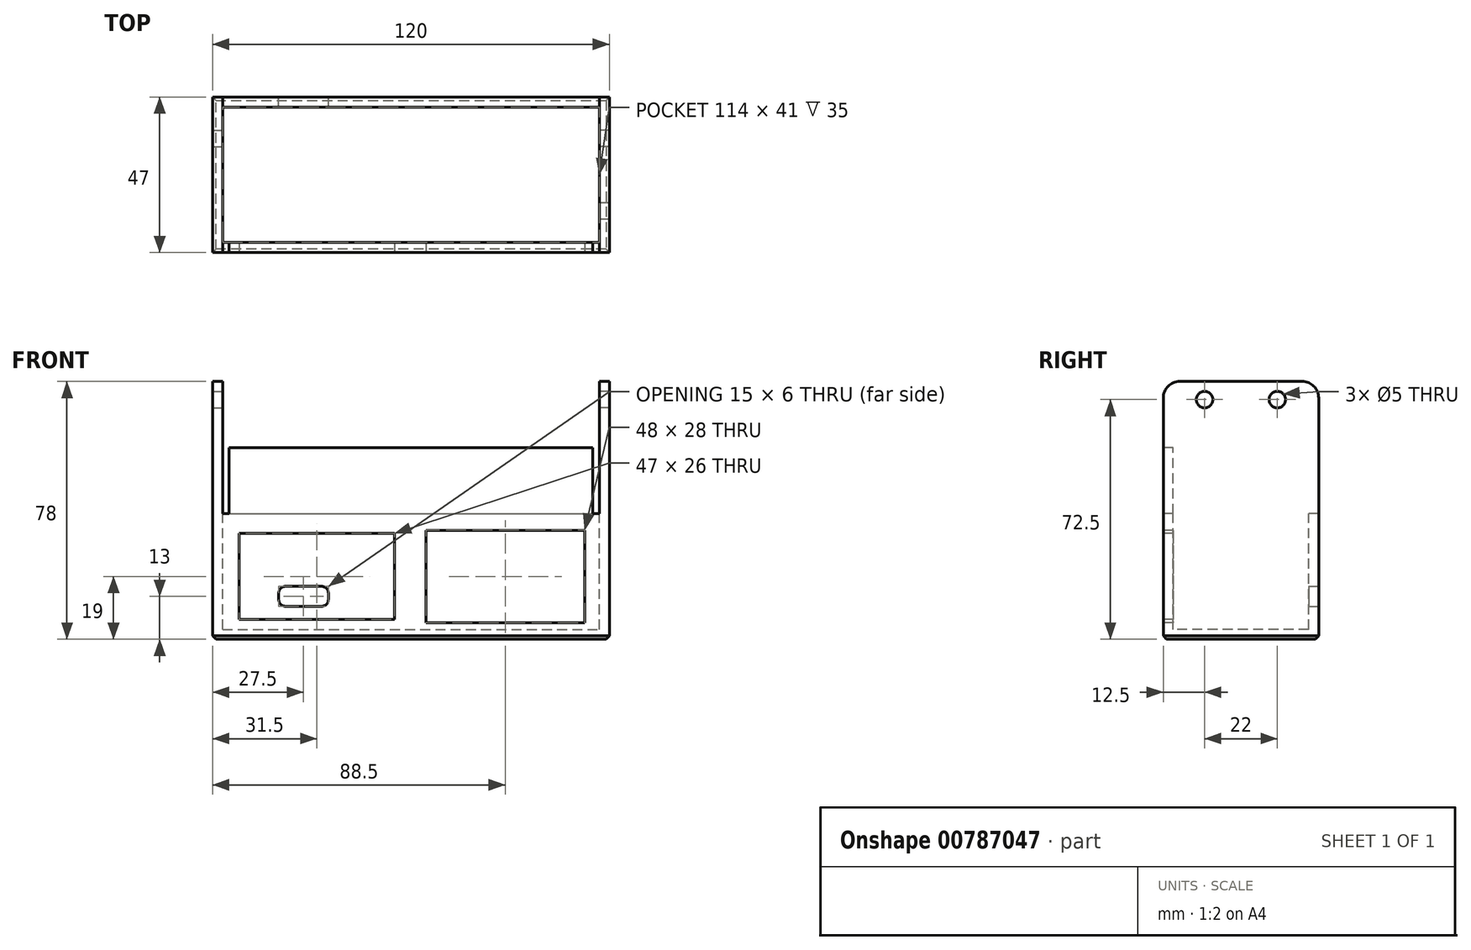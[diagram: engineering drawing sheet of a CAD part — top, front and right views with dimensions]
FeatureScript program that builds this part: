
annotation { "Feature Type Name" : "Feature", "Feature Type Description" : "" }
export const myFeature = defineFeature(function(context is Context, id is Id, definition is map)
    precondition{}
    {
        {
            assignVariable(context, id + "F0", {"name" : "wall", "anyValue" : 3});
        }
        {
            assignVariable(context, id + "F1", {"name" : "width", "anyValue" : 114});
        }
        {
            var Q0;
            Q0=qCreatedBy(makeId("Right.planeOp"),FACE);
            var sketch = newSketch(context, id + "F2", { "sketchPlane" : qUnion([Q0])});
            skLineSegment(sketch, "E0.bottom", {"start": v(17.5, 40) * mm, "end": v(-19.5, 40) * mm});
            skLineSegment(sketch, "E0.top", {"start": v(22.5, -38) * mm, "end": v(-24.5, -38) * mm});
            skLineSegment(sketch, "E0.left", {"start": v(22.5, 35) * mm, "end": v(22.5, -38) * mm});
            skLineSegment(sketch, "E0.right", {"start": v(-24.5, 35) * mm, "end": v(-24.5, -38) * mm});
            skCircle(sketch, "E1", {"center": v(10, 34.5) * mm, "radius": 2.5 * mm});
            skCircle(sketch, "E2", {"center": v(-12, 34.5) * mm, "radius": 2.5 * mm});
            skPoint(sketch, "E3.visualSharp", {"position": v(-24.5, 40) * mm});
            skArc(sketch, "E3.filletArc", {"start": v(-19.5, 40) * mm, "mid": v(-23.04, 38.54) * mm, "end": v(-24.5, 35) * mm});
            skPoint(sketch, "E4.visualSharp", {"position": v(22.5, 40) * mm});
            skArc(sketch, "E4.filletArc", {"start": v(22.5, 35) * mm, "mid": v(21.04, 38.54) * mm, "end": v(17.5, 40) * mm});
            skSolve(sketch);
        }
        {
            var Q0;
            Q0=qSketchRegion(id+"F2",true);
            extrude(context, id + "F3", {"entities" : qUnion([Q0]), "depth" : (getVariable(context, 'wall')) * mm, "offsetDistance" : 25 * mm});
        }
        {
            var Q0;
            Q0=qCreatedBy(makeId("Right.planeOp"),FACE);
            var sketch = newSketch(context, id + "F4", { "sketchPlane" : qUnion([Q0])});
            skLineSegment(sketch, "E5.bottom", {"start": v(22.5, -38) * mm, "end": v(-24.5, -38) * mm});
            skLineSegment(sketch, "E5.top", {"start": v(22.5, -35) * mm, "end": v(-24.5, -35) * mm});
            skLineSegment(sketch, "E5.left", {"start": v(22.5, -38) * mm, "end": v(22.5, -35) * mm});
            skLineSegment(sketch, "E5.right", {"start": v(-24.5, -38) * mm, "end": v(-24.5, -35) * mm});
            skLineSegment(sketch, "E6.bottom", {"start": v(-24.5, -38) * mm, "end": v(-21.5, -38) * mm});
            skLineSegment(sketch, "E6.top", {"start": v(-24.5, 0) * mm, "end": v(-21.5, 0) * mm});
            skLineSegment(sketch, "E6.left", {"start": v(-24.5, -38) * mm, "end": v(-24.5, 0) * mm});
            skLineSegment(sketch, "E6.right", {"start": v(-21.5, -38) * mm, "end": v(-21.5, 0) * mm});
            skLineSegment(sketch, "E7.bottom", {"start": v(22.5, -38) * mm, "end": v(19.5, -38) * mm});
            skLineSegment(sketch, "E7.top", {"start": v(22.5, 0) * mm, "end": v(19.5, 0) * mm});
            skLineSegment(sketch, "E7.left", {"start": v(22.5, -38) * mm, "end": v(22.5, 0) * mm});
            skLineSegment(sketch, "E7.right", {"start": v(19.5, -38) * mm, "end": v(19.5, 0) * mm});
            skSolve(sketch);
        }
        {
            var Q0;
            {var subQ0=sQuery(id+"F4.wireOp",EDGE,"E5.right");var subQ1=sQuery(id+"F4.wireOp",EDGE,"E5.bottom");var subQ9=sQuery(id+"F4.wireOp",EDGE,"E7.right");var subQ10=makeQuery(id+"F4.imprint","INTERSECT",VERTEX,{"derivedFrom":[subQ1,subQ9]});var subQ14=sQuery(id+"F4.wireOp",EDGE,"E5.left");var subQ16=sQuery(id+"F4.wireOp",EDGE,"E7.top");var subQ17=sQuery(id+"F4.wireOp",EDGE,"E6.top");Q0=qUnion([makeQuery(id+"F4.imprint","IMPRINT",FACE,{"disambiguationData":[TD([[makeQuery(id+"F4.imprint","IMPRINT",EDGE,{"derivedFrom":subQ17}),-1.0]])]}),makeQuery(id+"F4.imprint","IMPRINT",FACE,{"disambiguationData":[TD([[makeQuery(id+"F4.imprint","IMPRINT",EDGE,{"derivedFrom":subQ14}),1.0]])]}),makeQuery(id+"F4.imprint","IMPRINT",FACE,{"disambiguationData":[TD([[makeQuery(id+"F4.imprint","IMPRINT",EDGE,{"derivedFrom":subQ16}),1.0]])]}),makeQuery(id+"F4.imprint","IMPRINT",FACE,{"disambiguationData":[TD([[makeQuery(id+"F4.imprint","IMPRINT",EDGE,{"disambiguationData":[TD([[subQ10,-1.0]])],"derivedFrom":subQ1}),-1.0]])]}),makeQuery(id+"F4.imprint","IMPRINT",FACE,{"disambiguationData":[TD([[makeQuery(id+"F4.imprint","IMPRINT",EDGE,{"derivedFrom":subQ0}),-1.0]])]})]);}
            extrude(context, id + "F5", {"entities" : qUnion([Q0]), "operationType" : NewBodyOperationType.ADD, "oppositeDirection" : true, "depth" : (getVariable(context, 'width')) * mm, "offsetDistance" : 25 * mm});
        }
        {
            var Q0;
            Q0=makeQuery(id+"F5.opExtrude","CAP_FACE",FACE,{"disambiguationData":[OSD([sQuery(id+"F4.wireOp",EDGE,"E5.bottom"),sQuery(id+"F4.wireOp",EDGE,"E5.top"),sQuery(id+"F4.wireOp",EDGE,"E5.left"),sQuery(id+"F4.wireOp",EDGE,"E5.right"),sQuery(id+"F4.wireOp",EDGE,"E6.top"),sQuery(id+"F4.wireOp",EDGE,"E6.left"),sQuery(id+"F4.wireOp",EDGE,"E6.right"),sQuery(id+"F4.wireOp",EDGE,"E7.top"),sQuery(id+"F4.wireOp",EDGE,"E7.left"),sQuery(id+"F4.wireOp",EDGE,"E7.right")])],"isStart":false});
            var sketch = newSketch(context, id + "F6", { "sketchPlane" : qUnion([Q0])});
            skLineSegment(sketch, "E8.bottom", {"start": v(19.5, 40) * mm, "end": v(-17.5, 40) * mm});
            skLineSegment(sketch, "E8.top", {"start": v(24.5, -38) * mm, "end": v(-22.5, -38) * mm});
            skLineSegment(sketch, "E8.left", {"start": v(24.5, 35) * mm, "end": v(24.5, -38) * mm});
            skLineSegment(sketch, "E8.right", {"start": v(-22.5, 35) * mm, "end": v(-22.5, -38) * mm});
            skCircle(sketch, "E9", {"center": v(-10, 34.5) * mm, "radius": 2.5 * mm});
            skPoint(sketch, "E10.visualSharp", {"position": v(-22.5, 40) * mm});
            skArc(sketch, "E10.filletArc", {"start": v(-17.5, 40) * mm, "mid": v(-21.04, 38.54) * mm, "end": v(-22.5, 35) * mm});
            skPoint(sketch, "E11.visualSharp", {"position": v(24.5, 40) * mm});
            skArc(sketch, "E11.filletArc", {"start": v(24.5, 35) * mm, "mid": v(23.04, 38.54) * mm, "end": v(19.5, 40) * mm});
            skSolve(sketch);
        }
        {
            var Q0;
            Q0=qSketchRegion(id+"F6",true);
            extrude(context, id + "F7", {"entities" : qUnion([Q0]), "operationType" : NewBodyOperationType.ADD, "depth" : (getVariable(context, 'wall')) * mm, "offsetDistance" : 25 * mm});
        }
        {
            var Q0;
            Q0=makeQuery(id+"F7.boolean.opBoolean","MERGE",FACE,{"derivedFrom":[makeQuery(id+"F5.boolean.opBoolean","MERGE",FACE,{"derivedFrom":[makeQuery(id+"F3.opExtrude","SWEPT_FACE",FACE,{"disambiguationData":[OSD([sQuery(id+"F2.wireOp",EDGE,"E0.right")])]}),makeQuery(id+"F5.opExtrude","SWEPT_FACE",FACE,{"disambiguationData":[OSD([sQuery(id+"F4.wireOp",EDGE,"E5.right"),sQuery(id+"F4.wireOp",EDGE,"E6.left")])]})]}),makeQuery(id+"F7.opExtrude","SWEPT_FACE",FACE,{"disambiguationData":[OSD([sQuery(id+"F6.wireOp",EDGE,"E8.left")])]})]});
            var sketch = newSketch(context, id + "F8", { "sketchPlane" : qUnion([Q0])});
            skLineSegment(sketch, "E12.bottom", {"start": v(-112, 0) * mm, "end": v(-2, 0) * mm});
            skLineSegment(sketch, "E12.top", {"start": v(-112, 20) * mm, "end": v(-2, 20) * mm});
            skLineSegment(sketch, "E12.left", {"start": v(-112, 0) * mm, "end": v(-112, 20) * mm});
            skLineSegment(sketch, "E12.right", {"start": v(-2, 0) * mm, "end": v(-2, 20) * mm});
            skSolve(sketch);
        }
        {
            var Q0;
            Q0=qSketchRegion(id+"F8",true);
            extrude(context, id + "F9", {"entities" : qUnion([Q0]), "operationType" : NewBodyOperationType.ADD, "oppositeDirection" : true, "depth" : (getVariable(context, 'wall')) * mm, "offsetDistance" : 25 * mm});
        }
        {
            var Q0;
            {var subQ2=sQuery(id+"F8.wireOp",EDGE,"E12.bottom");Q0=makeQuery(id+"F8.imprint","IMPRINT",FACE,{"disambiguationData":[TD([[makeQuery(id+"F8.imprint","IMPRINT",EDGE,{"derivedFrom":subQ2}),-1.0]])]});}
            var sketch = newSketch(context, id + "F10", { "sketchPlane" : qUnion([Q0])});
            skLineSegment(sketch, "E13.bottom", {"start": v(-109, -6) * mm, "end": v(-62, -6) * mm});
            skLineSegment(sketch, "E13.top", {"start": v(-109, -32) * mm, "end": v(-62, -32) * mm});
            skLineSegment(sketch, "E13.left", {"start": v(-109, -6) * mm, "end": v(-109, -32) * mm});
            skLineSegment(sketch, "E13.right", {"start": v(-62, -6) * mm, "end": v(-62, -32) * mm});
            skLineSegment(sketch, "E14.bottom", {"start": v(-52.5, -5) * mm, "end": v(-4.5, -5) * mm});
            skLineSegment(sketch, "E14.top", {"start": v(-52.5, -33) * mm, "end": v(-4.5, -33) * mm});
            skLineSegment(sketch, "E14.left", {"start": v(-52.5, -5) * mm, "end": v(-52.5, -33) * mm});
            skLineSegment(sketch, "E14.right", {"start": v(-4.5, -5) * mm, "end": v(-4.5, -33) * mm});
            skLineSegment(sketch, "E15", {"start": v(-57, 0) * mm, "end": v(-57, -48.8) * mm, "construction": true});
            skLineSegment(sketch, "E16", {"start": v(-121.46, -19) * mm, "end": v(11.47, -19) * mm, "construction": true});
            skSolve(sketch);
        }
        {
            var Q0;
            Q0=qSketchRegion(id+"F10",true);
            extrude(context, id + "F11", {"entities" : qUnion([Q0]), "operationType" : NewBodyOperationType.REMOVE, "endBound" : BoundingType.UP_TO_NEXT, "oppositeDirection" : true, "depth" : 25 * mm, "offsetDistance" : 25 * mm});
        }
        {
            var Q0;
            Q0=makeQuery(id+"F7.boolean.opBoolean","MERGE",FACE,{"derivedFrom":[makeQuery(id+"F5.boolean.opBoolean","MERGE",FACE,{"derivedFrom":[makeQuery(id+"F3.opExtrude","SWEPT_FACE",FACE,{"disambiguationData":[OSD([sQuery(id+"F2.wireOp",EDGE,"E0.left")])]}),makeQuery(id+"F5.opExtrude","SWEPT_FACE",FACE,{"disambiguationData":[OSD([sQuery(id+"F4.wireOp",EDGE,"E5.left"),sQuery(id+"F4.wireOp",EDGE,"E7.left")])]})]}),makeQuery(id+"F7.opExtrude","SWEPT_FACE",FACE,{"disambiguationData":[OSD([sQuery(id+"F6.wireOp",EDGE,"E8.right")])]})]});
            var sketch = newSketch(context, id + "F12", { "sketchPlane" : qUnion([Q0])});
            skLineSegment(sketch, "E17.bottom", {"start": v(84, -28) * mm, "end": v(95, -28) * mm});
            skLineSegment(sketch, "E17.top", {"start": v(84, -22) * mm, "end": v(95, -22) * mm});
            skLineSegment(sketch, "E17.left", {"start": v(82, -26) * mm, "end": v(82, -24) * mm});
            skLineSegment(sketch, "E17.right", {"start": v(97, -26) * mm, "end": v(97, -24) * mm});
            skPoint(sketch, "E18.visualSharp", {"position": v(82, -28) * mm});
            skArc(sketch, "E18.filletArc", {"start": v(82, -26) * mm, "mid": v(82.59, -27.41) * mm, "end": v(84, -28) * mm});
            skPoint(sketch, "E19.visualSharp", {"position": v(82, -22) * mm});
            skArc(sketch, "E19.filletArc", {"start": v(84, -22) * mm, "mid": v(82.59, -22.59) * mm, "end": v(82, -24) * mm});
            skPoint(sketch, "E20.visualSharp", {"position": v(97, -22) * mm});
            skArc(sketch, "E20.filletArc", {"start": v(97, -24) * mm, "mid": v(96.41, -22.59) * mm, "end": v(95, -22) * mm});
            skPoint(sketch, "E21.visualSharp", {"position": v(97, -28) * mm});
            skArc(sketch, "E21.filletArc", {"start": v(95, -28) * mm, "mid": v(96.41, -27.41) * mm, "end": v(97, -26) * mm});
            skSolve(sketch);
        }
        {
            var Q0;
            Q0=qSketchRegion(id+"F12",true);
            extrude(context, id + "F13", {"entities" : qUnion([Q0]), "operationType" : NewBodyOperationType.REMOVE, "endBound" : BoundingType.UP_TO_NEXT, "oppositeDirection" : true, "depth" : 25 * mm, "offsetDistance" : 25 * mm});
        }
        {
            var Q0;
            Q0=makeQuery(id+"F7.boolean.opBoolean","MERGE",FACE,{"derivedFrom":[makeQuery(id+"F5.boolean.opBoolean","MERGE",FACE,{"derivedFrom":[makeQuery(id+"F3.opExtrude","SWEPT_FACE",FACE,{"disambiguationData":[OSD([sQuery(id+"F2.wireOp",EDGE,"E0.top")])]}),makeQuery(id+"F5.opExtrude","SWEPT_FACE",FACE,{"disambiguationData":[OSD([sQuery(id+"F4.wireOp",EDGE,"E5.bottom")])]})]}),makeQuery(id+"F7.opExtrude","SWEPT_FACE",FACE,{"disambiguationData":[OSD([sQuery(id+"F6.wireOp",EDGE,"E8.top")])]})]});
            chamfer(context, id + "F14", {"entities" : qUnion([Q0]), "width" : 1 * mm, "tangentPropagation" : true});
        }
    });
